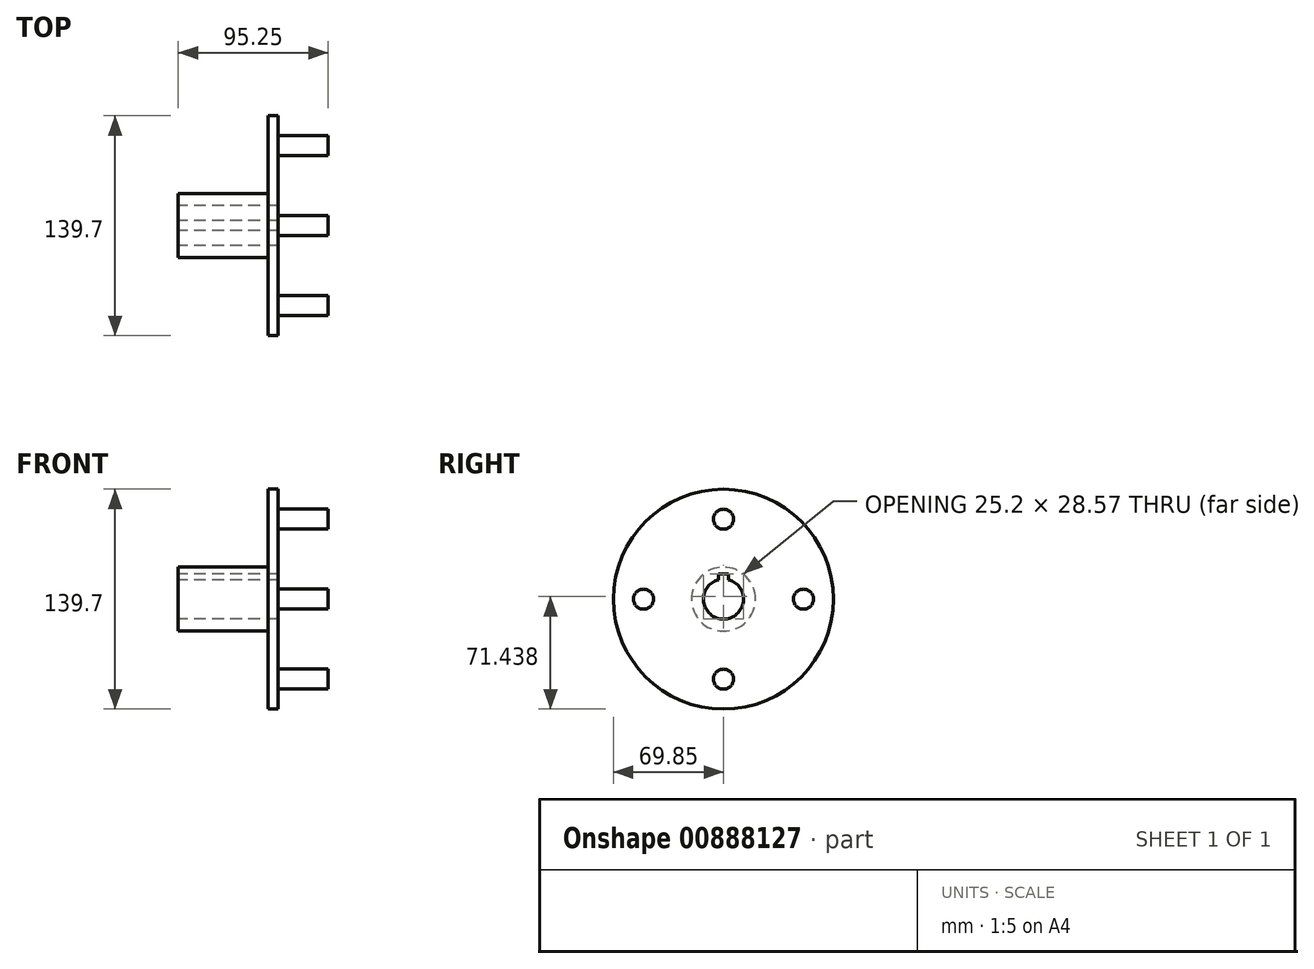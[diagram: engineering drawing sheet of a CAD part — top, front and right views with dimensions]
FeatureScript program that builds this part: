
annotation { "Feature Type Name" : "Feature", "Feature Type Description" : "" }
export const myFeature = defineFeature(function(context is Context, id is Id, definition is map)
    precondition{}
    {
        {
            var Q0;
            Q0=qCreatedBy(makeId("Front.planeOp"),FACE);
            var sketch = newSketch(context, id + "F0", { "sketchPlane" : qUnion([Q0])});
            skLineSegment(sketch, "E0", {"start": v(0, 12.7) * mm, "end": v(0, 20.32) * mm});
            skLineSegment(sketch, "E1", {"start": v(0, 20.32) * mm, "end": v(57.15, 20.32) * mm});
            skLineSegment(sketch, "E2", {"start": v(57.15, 20.32) * mm, "end": v(57.15, 69.85) * mm});
            skLineSegment(sketch, "E3", {"start": v(57.15, 69.85) * mm, "end": v(63.5, 69.85) * mm});
            skLineSegment(sketch, "E4", {"start": v(63.5, 69.85) * mm, "end": v(63.5, 12.7) * mm});
            skLineSegment(sketch, "E5", {"start": v(63.5, 12.7) * mm, "end": v(0, 12.7) * mm});
            skLineSegment(sketch, "E6", {"start": v(0, 0) * mm, "end": v(63.5, 0) * mm, "construction": true});
            skSolve(sketch);
        }
        {
            var Q0;
            Q0 = qSketchRegion(id + "F0", true);
            var Q1;
            Q1=sQuery(id+"F0.wireOp",EDGE,"E6");
            revolve(context, id + "F1", {"surfaceOperationType" : NewSurfaceOperationType.NEW, "entities" : qUnion([Q0]), "axis" : qUnion([Q1]), "revolveType" : RevolveType.FULL});
        }
        {
            var Q0;
            Q0=qCreatedBy(makeId("Right.planeOp"),FACE);
            var sketch = newSketch(context, id + "F2", { "sketchPlane" : qUnion([Q0])});
            skCircle(sketch, "E7.0", {"center": v(0, 0) * mm, "radius": 12.7 * mm, "construction": true});
            skLineSegment(sketch, "E8", {"start": v(0, 0) * mm, "end": v(0, 12.7) * mm, "construction": true});
            skLineSegment(sketch, "E9.bottom", {"start": v(3.18, 15.88) * mm, "end": v(-3.18, 15.88) * mm});
            skLineSegment(sketch, "E9.top", {"start": v(3.18, 9.53) * mm, "end": v(-3.17, 9.53) * mm});
            skLineSegment(sketch, "E9.left", {"start": v(3.18, 15.88) * mm, "end": v(3.18, 9.53) * mm});
            skLineSegment(sketch, "E9.right", {"start": v(-3.18, 15.88) * mm, "end": v(-3.17, 9.53) * mm});
            skPoint(sketch, "E9.middle", {"position": v(0, 12.7) * mm});
            skSolve(sketch);
        }
        {
            var Q0;
            Q0 = qSketchRegion(id + "F2", true);
            extrude(context, id + "F3", {"entities" : qUnion([Q0]), "operationType" : NewBodyOperationType.REMOVE, "endBound" : BoundingType.THROUGH_ALL, "depth" : 25.4 * mm, "offsetDistance" : 25.4 * mm});
        }
        {
            var Q0;
            Q0=makeQuery(id+"F1.opRevolve","SWEPT_FACE",FACE,{"disambiguationData":[OSD([sQuery(id+"F0.wireOp",EDGE,"E4")])]});
            var sketch = newSketch(context, id + "F4", { "sketchPlane" : qUnion([Q0])});
            skLineSegment(sketch, "E10", {"start": v(0, 0) * mm, "end": v(0, 50.8) * mm, "construction": true});
            skCircle(sketch, "E11", {"center": v(0, 50.8) * mm, "radius": 6.35 * mm});
            skCircle(sketch, "E12.1.0", {"center": v(-50.8, 0) * mm, "radius": 6.35 * mm});
            skCircle(sketch, "E12.2.0", {"center": v(0, -50.8) * mm, "radius": 6.35 * mm});
            skCircle(sketch, "E12.3.0", {"center": v(50.8, 0) * mm, "radius": 6.35 * mm});
            skPoint(sketch, "E12.center", {"position": v(0, 0) * mm});
            skSolve(sketch);
        }
        {
            var Q0;
            Q0 = qSketchRegion(id + "F4", true);
            extrude(context, id + "F5", {"entities" : qUnion([Q0]), "operationType" : NewBodyOperationType.ADD, "depth" : 31.75 * mm, "offsetDistance" : 25.4 * mm});
        }
    });
